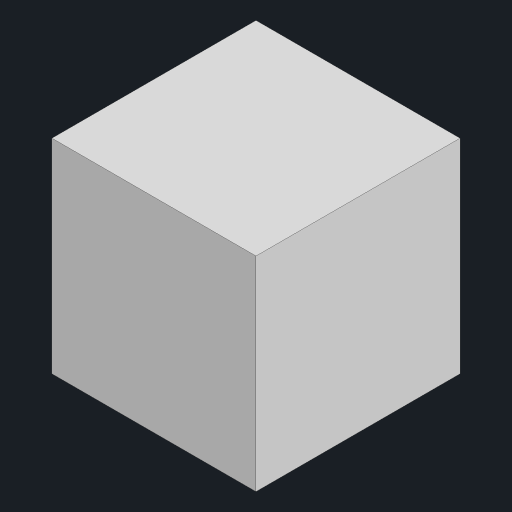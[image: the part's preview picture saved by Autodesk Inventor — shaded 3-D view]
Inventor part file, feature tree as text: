
AUTODESK INVENTOR PART (.ipt)
format: ipt  version: 2023.4 (Build 274418000, 418)  size: 79,872 bytes
history: native  units: in
note: dims shown in document units (in); Inventor stores cm internally (conversion verified against a paired STEP export)
features: extrude x1, sketch x1
ambient origin geometry x8: Origin, YZ Plane, XZ Plane, XY Plane, X Axis, Y Axis, Z Axis, Center Point
bodies: Solid1 (feature_tree)
feature tree (2):
  extrude  "Extrusion1"  Depth=1.1811in
  sketch  "Sketch1"  dims[d0=1.1811in d1=1.1811in d2=1.1811in d3=0.0in]
